# Revit family: RN 90032 Optifitt-Serra-Rohrnippel
name_source: partatom
category: Rohrformteile
units: mm (PartAtom-declared; Revit-internal decimal feet)

## family parameters
Arbeitsebenenbasiert = Nein
Beim Laden mit Abzugskörper schneiden = Nein
Bemaßung runder Anschluss = Durchmesser verwenden
Gemeinsam genutzt = Nein
Immer vertikal = Ja
Teiletyp = Nicht definiert

## types (17) — shared parameters
1.010.00.2 Blattnummer der Richtlinie = 29
1.010.00.3 Ausgabedatum (Monat) der Richtlinie = 201308
1.010.00.4 Herstellername = R. Nussbaum AG
1.010.00.5 Revisionsdatum der Datei = 20190521
1.010.00.6 Webadresse des Herstellers = http://www.nussbaum.ch
1.100.00.4 Produktbezeichnung = Versorgung
1.110.00.2 Index = 3
1.110.00.4 Produktbezeichnung = Optifitt-Serra
1.960/3L.00.8 Link (URL) = https://www.nussbaum.ch
29.700.00.4 Produktname = Optifitt-Serra-Rohrnippel
29.700.00.5 Produktkennung = 2
29.700.00.6 Querschnittsform = 1
29.700.00.7 Nennweitensystem = DN
29.700.00.8 Nenndrucksystem = PN
29.710.02.4 Nenndruck = 16
29.710.02.5 max. zul. Überdruck [hPa] = 1600
29.710.02.7 max. zul. Dauer-Betriebsdruck [hPa] = 1600
29.710.02.9 max. zul. Dauer-Betriebstemperatur [°C] = 90
Connector Visibility = Nein
EnclosingSpace Visibility = Nein
R. Nussbaum AG 90032.22 de Visibility = Nein
R. Nussbaum AG 90032.24 de Visibility = Nein
R. Nussbaum AG 90032.26 de Visibility = Nein
R. Nussbaum AG 90032.28 de Visibility = Nein
R. Nussbaum AG 90032.30 de Visibility = Nein
R. Nussbaum AG 90032.32 de Visibility = Nein
R. Nussbaum AG 90032.34 de Visibility = Nein
R. Nussbaum AG 90032.38 de Visibility = Nein
R. Nussbaum AG 90032.39 de Visibility = Nein
R. Nussbaum AG 90032.41 de Visibility = Nein
R. Nussbaum AG 90032.42 de Visibility = Nein
R. Nussbaum AG 90032.44 de Visibility = Nein
R. Nussbaum AG 90032.45 de Visibility = Nein
R. Nussbaum AG 90032.46 de Visibility = Nein
R. Nussbaum AG 90032.49 de Visibility = Nein
R. Nussbaum AG 90032.51 de Visibility = Nein
R. Nussbaum AG 90032.52 de Visibility = Nein
R. Nussbaum AG 90032.53 de Visibility = Nein
R. Nussbaum AG 90032.54 de Visibility = Nein
R. Nussbaum AG 90032.56 de Visibility = Nein
R. Nussbaum AG 90032.58 de Visibility = Nein
R. Nussbaum AG 90032.59 de Visibility = Nein
R. Nussbaum AG 90032.61 de Visibility = Nein
R. Nussbaum AG 90032.62 de Visibility = Nein
R. Nussbaum AG 90032.63 de Visibility = Nein
R. Nussbaum AG 90032.64 de Visibility = Nein
R. Nussbaum AG 90032.66 de Visibility = Nein
R. Nussbaum AG 90032.67 de Visibility = Nein
R. Nussbaum AG 90032.68 de Visibility = Nein
R. Nussbaum AG 90032.69 de Visibility = Nein
R. Nussbaum AG 90032.71 de Visibility = Nein
R. Nussbaum AG 90032.72 de Visibility = Nein
R. Nussbaum AG 90032.74 de Visibility = Nein
R. Nussbaum AG 90032.75 de Visibility = Nein
R. Nussbaum AG 90032.78 de Visibility = Nein
R. Nussbaum AG 90032.79 de Visibility = Nein
R. Nussbaum AG 90032.82 de Visibility = Nein
R. Nussbaum AG 90032.83 de Visibility = Nein
R. Nussbaum AG 90032.86 de Visibility = Nein
R. Nussbaum AG 90032.87 de Visibility = Nein
R. Nussbaum AG 90032.89 de Visibility = Nein
R. Nussbaum AG 90032.90 de Visibility = Nein
R. Nussbaum AG 90032.91 de Visibility = Nein
R. Nussbaum AG 90032.94 de Visibility = Nein
R. Nussbaum AG 90032.95 de Visibility = Nein
R. Nussbaum AG 90032.96 de Visibility = Nein
R. Nussbaum AG 90032.97 de Visibility = Nein

## per-type parameters (varying)
- DN=40: 1.800.00.3 TGA-Nummer=01900300000000000000000000000000000000000000000019000000000000000048; 1.800.00.4 Kommentarfeld=90032.88, Optifitt-Serra-Rohrnippel, DN=40, L=100, R=1½; 1.810.00.3 Hersteller-Bestellnummer=90032.88; 1.810.00.4 DATANORM-Nummer=90032.88; 1.810.00.5 StLB-Nummer=214.236; 1.810.00.6 GTIN-Nummer=7612945034571; 29.710.02.10 Formstück-Gewicht [kg]=0.459; 29.710.02.3 Benennung=Optifitt-Serra-Rohrnippel, DN=40, L=100, R=1½; CONNECTOR0_DIAMETER_dX_0r=40 mm; CONNECTOR0_dX_01=19 mm  [stored 0.062336 ft]; CONNECTOR0_ref_dX=19 mm  [stored 0.062336 ft]; CONNECTOR1_DIAMETER_dX_0r=40 mm; CONNECTOR1_dX_00=79 mm; CONNECTOR1_dX_01=98 mm; CONNECTOR1_ref_dX=79 mm; CONNECTOR1_ref_dX2=98 mm; R. Nussbaum AG 90032.36 de Visibility=Nein; R. Nussbaum AG 90032.37 de Visibility=Nein; R. Nussbaum AG 90032.40 de Visibility=Nein; R. Nussbaum AG 90032.47 de Visibility=Nein; R. Nussbaum AG 90032.48 de Visibility=Nein; R. Nussbaum AG 90032.50 de Visibility=Nein; R. Nussbaum AG 90032.55 de Visibility=Nein; R. Nussbaum AG 90032.57 de Visibility=Nein; R. Nussbaum AG 90032.60 de Visibility=Nein; R. Nussbaum AG 90032.65 de Visibility=Nein; R. Nussbaum AG 90032.70 de Visibility=Nein; R. Nussbaum AG 90032.80 de Visibility=Nein; R. Nussbaum AG 90032.81 de Visibility=Nein; R. Nussbaum AG 90032.88 de Visibility=Ja; R. Nussbaum AG 90032.93 de Visibility=Nein; R. Nussbaum AG 90032.98 de Visibility=Nein; R. Nussbaum AG 90032.99 de Visibility=Nein
- DN=4: 1.800.00.3 TGA-Nummer=01900300000000000000000000000000000000000000000019000000000000000073; 1.800.00.4 Kommentarfeld=90032.80, Optifitt-Serra-Rohrnippel, DN=32, L=100, R=1¼; 1.810.00.3 Hersteller-Bestellnummer=90032.8; 1.810.00.4 DATANORM-Nummer=90032.8; 1.810.00.5 StLB-Nummer=214.235; 1.810.00.6 GTIN-Nummer=7612945034519; 29.710.02.10 Formstück-Gewicht [kg]=0.41; 29.710.02.3 Benennung=Optifitt-Serra-Rohrnippel, DN=32, L=100, R=1¼; CONNECTOR0_DIAMETER_dX_0r=32 mm  [stored 0.104987 ft]; CONNECTOR0_dX_01=19 mm  [stored 0.062336 ft]; CONNECTOR0_ref_dX=19 mm  [stored 0.062336 ft]; CONNECTOR1_DIAMETER_dX_0r=32 mm  [stored 0.104987 ft]; CONNECTOR1_dX_00=79 mm; CONNECTOR1_dX_01=98 mm; CONNECTOR1_ref_dX=79 mm; CONNECTOR1_ref_dX2=98 mm; Hersteller=R. Nussbaum AG; Modell=90032.8; R. Nussbaum AG 90032.36 de Visibility=Nein; R. Nussbaum AG 90032.37 de Visibility=Nein; R. Nussbaum AG 90032.40 de Visibility=Nein; R. Nussbaum AG 90032.47 de Visibility=Nein; R. Nussbaum AG 90032.48 de Visibility=Nein; R. Nussbaum AG 90032.50 de Visibility=Nein; R. Nussbaum AG 90032.55 de Visibility=Nein; R. Nussbaum AG 90032.57 de Visibility=Nein; R. Nussbaum AG 90032.60 de Visibility=Nein; R. Nussbaum AG 90032.65 de Visibility=Nein; R. Nussbaum AG 90032.70 de Visibility=Nein; R. Nussbaum AG 90032.80 de Visibility=Ja; R. Nussbaum AG 90032.81 de Visibility=Nein; R. Nussbaum AG 90032.88 de Visibility=Nein; R. Nussbaum AG 90032.93 de Visibility=Nein; R. Nussbaum AG 90032.98 de Visibility=Nein; R. Nussbaum AG 90032.99 de Visibility=Nein; Typenkommentare=Optifitt-Serra-Rohrnippel  DN=32; URL=https://www.nussbaum.ch
- DN=3: 1.800.00.3 TGA-Nummer=01900300000000000000000000000000000000000000000019000000000000000072; 1.800.00.4 Kommentarfeld=90032.70, Optifitt-Serra-Rohrnippel, DN=25, L=100, R=1; 1.810.00.3 Hersteller-Bestellnummer=90032.7; 1.810.00.4 DATANORM-Nummer=90032.7; 1.810.00.5 StLB-Nummer=214.234; 1.810.00.6 GTIN-Nummer=7612945034458; 29.710.02.10 Formstück-Gewicht [kg]=0.287; 29.710.02.3 Benennung=Optifitt-Serra-Rohrnippel, DN=25, L=100, R=1; CONNECTOR0_DIAMETER_dX_0r=25 mm  [stored 0.082021 ft]; CONNECTOR0_dX_01=17 mm; CONNECTOR0_ref_dX=17 mm; CONNECTOR1_DIAMETER_dX_0r=25 mm  [stored 0.082021 ft]; CONNECTOR1_dX_00=81 mm; CONNECTOR1_dX_01=98 mm; CONNECTOR1_ref_dX=81 mm; CONNECTOR1_ref_dX2=98 mm; Hersteller=R. Nussbaum AG; Modell=90032.7; R. Nussbaum AG 90032.36 de Visibility=Nein; R. Nussbaum AG 90032.37 de Visibility=Nein; R. Nussbaum AG 90032.40 de Visibility=Nein; R. Nussbaum AG 90032.47 de Visibility=Nein; R. Nussbaum AG 90032.48 de Visibility=Nein; R. Nussbaum AG 90032.50 de Visibility=Nein; R. Nussbaum AG 90032.55 de Visibility=Nein; R. Nussbaum AG 90032.57 de Visibility=Nein; R. Nussbaum AG 90032.60 de Visibility=Nein; R. Nussbaum AG 90032.65 de Visibility=Nein; R. Nussbaum AG 90032.70 de Visibility=Ja; R. Nussbaum AG 90032.80 de Visibility=Nein; R. Nussbaum AG 90032.81 de Visibility=Nein; R. Nussbaum AG 90032.88 de Visibility=Nein; R. Nussbaum AG 90032.93 de Visibility=Nein; R. Nussbaum AG 90032.98 de Visibility=Nein; R. Nussbaum AG 90032.99 de Visibility=Nein; Typenkommentare=Optifitt-Serra-Rohrnippel  DN=25; URL=https://www.nussbaum.ch
- DN=2: 1.800.00.3 TGA-Nummer=01900300000000000000000000000000000000000000000019000000000000000071; 1.800.00.4 Kommentarfeld=90032.60, Optifitt-Serra-Rohrnippel, DN=20, L=150, R=¾; 1.810.00.3 Hersteller-Bestellnummer=90032.6; 1.810.00.4 DATANORM-Nummer=90032.6; 1.810.00.6 GTIN-Nummer=7612945034380; 29.710.02.10 Formstück-Gewicht [kg]=0.325; 29.710.02.3 Benennung=Optifitt-Serra-Rohrnippel, DN=20, L=150, R=¾; CONNECTOR0_DIAMETER_dX_0r=20 mm  [stored 0.0656168 ft]; CONNECTOR0_dX_01=15 mm  [stored 0.0492126 ft]; CONNECTOR0_ref_dX=15 mm  [stored 0.0492126 ft]; CONNECTOR1_DIAMETER_dX_0r=20 mm  [stored 0.0656168 ft]; CONNECTOR1_dX_00=133 mm; CONNECTOR1_dX_01=148 mm; CONNECTOR1_ref_dX=133 mm; CONNECTOR1_ref_dX2=148 mm; Hersteller=R. Nussbaum AG; Modell=90032.6; R. Nussbaum AG 90032.36 de Visibility=Nein; R. Nussbaum AG 90032.37 de Visibility=Nein; R. Nussbaum AG 90032.40 de Visibility=Nein; R. Nussbaum AG 90032.47 de Visibility=Nein; R. Nussbaum AG 90032.48 de Visibility=Nein; R. Nussbaum AG 90032.50 de Visibility=Nein; R. Nussbaum AG 90032.55 de Visibility=Nein; R. Nussbaum AG 90032.57 de Visibility=Nein; R. Nussbaum AG 90032.60 de Visibility=Ja; R. Nussbaum AG 90032.65 de Visibility=Nein; R. Nussbaum AG 90032.70 de Visibility=Nein; R. Nussbaum AG 90032.80 de Visibility=Nein; R. Nussbaum AG 90032.81 de Visibility=Nein; R. Nussbaum AG 90032.88 de Visibility=Nein; R. Nussbaum AG 90032.93 de Visibility=Nein; R. Nussbaum AG 90032.98 de Visibility=Nein; R. Nussbaum AG 90032.99 de Visibility=Nein; Typenkommentare=Optifitt-Serra-Rohrnippel  DN=20; URL=https://www.nussbaum.ch
- DN=5: 1.800.00.3 TGA-Nummer=01900300000000000000000000000000000000000000000019000000000000000070; 1.800.00.4 Kommentarfeld=90032.50, Optifitt-Serra-Rohrnippel, DN=20, L=40, R=¾; 1.810.00.3 Hersteller-Bestellnummer=90032.5; 1.810.00.4 DATANORM-Nummer=90032.5; 1.810.00.5 StLB-Nummer=214.233; 1.810.00.6 GTIN-Nummer=7612945034328; 29.710.02.10 Formstück-Gewicht [kg]=0.072; 29.710.02.3 Benennung=Optifitt-Serra-Rohrnippel, DN=20, L=40, R=¾; CONNECTOR0_DIAMETER_dX_0r=20 mm  [stored 0.0656168 ft]; CONNECTOR0_dX_01=15 mm  [stored 0.0492126 ft]; CONNECTOR0_ref_dX=15 mm  [stored 0.0492126 ft]; CONNECTOR1_DIAMETER_dX_0r=20 mm  [stored 0.0656168 ft]; CONNECTOR1_dX_00=23 mm  [stored 0.0754593 ft]; CONNECTOR1_dX_01=38 mm; CONNECTOR1_ref_dX=23 mm  [stored 0.0754593 ft]; CONNECTOR1_ref_dX2=38 mm; Hersteller=R. Nussbaum AG; Modell=90032.5; R. Nussbaum AG 90032.36 de Visibility=Nein; R. Nussbaum AG 90032.37 de Visibility=Nein; R. Nussbaum AG 90032.40 de Visibility=Nein; R. Nussbaum AG 90032.47 de Visibility=Nein; R. Nussbaum AG 90032.48 de Visibility=Nein; R. Nussbaum AG 90032.50 de Visibility=Ja; R. Nussbaum AG 90032.55 de Visibility=Nein; R. Nussbaum AG 90032.57 de Visibility=Nein; R. Nussbaum AG 90032.60 de Visibility=Nein; R. Nussbaum AG 90032.65 de Visibility=Nein; R. Nussbaum AG 90032.70 de Visibility=Nein; R. Nussbaum AG 90032.80 de Visibility=Nein; R. Nussbaum AG 90032.81 de Visibility=Nein; R. Nussbaum AG 90032.88 de Visibility=Nein; R. Nussbaum AG 90032.93 de Visibility=Nein; R. Nussbaum AG 90032.98 de Visibility=Nein; R. Nussbaum AG 90032.99 de Visibility=Nein; Typenkommentare=Optifitt-Serra-Rohrnippel  DN=20; URL=https://www.nussbaum.ch
- DN=7: 1.800.00.3 TGA-Nummer=01900300000000000000000000000000000000000000000019000000000000000069; 1.800.00.4 Kommentarfeld=90032.40, Optifitt-Serra-Rohrnippel, DN=15, L=80, R=½; 1.810.00.3 Hersteller-Bestellnummer=90032.4; 1.810.00.4 DATANORM-Nummer=90032.4; 1.810.00.6 GTIN-Nummer=7612945034243; 29.710.02.10 Formstück-Gewicht [kg]=0.13; 29.710.02.3 Benennung=Optifitt-Serra-Rohrnippel, DN=15, L=80, R=½; CONNECTOR0_DIAMETER_dX_0r=15 mm  [stored 0.0492126 ft]; CONNECTOR0_dX_01=13 mm; CONNECTOR0_ref_dX=13 mm; CONNECTOR1_DIAMETER_dX_0r=15 mm  [stored 0.0492126 ft]; CONNECTOR1_dX_00=65 mm; CONNECTOR1_dX_01=78 mm  [stored 0.255906 ft]; CONNECTOR1_ref_dX=65 mm; CONNECTOR1_ref_dX2=78 mm  [stored 0.255906 ft]; Hersteller=R. Nussbaum AG; Modell=90032.4; R. Nussbaum AG 90032.36 de Visibility=Nein; R. Nussbaum AG 90032.37 de Visibility=Nein; R. Nussbaum AG 90032.40 de Visibility=Ja; R. Nussbaum AG 90032.47 de Visibility=Nein; R. Nussbaum AG 90032.48 de Visibility=Nein; R. Nussbaum AG 90032.50 de Visibility=Nein; R. Nussbaum AG 90032.55 de Visibility=Nein; R. Nussbaum AG 90032.57 de Visibility=Nein; R. Nussbaum AG 90032.60 de Visibility=Nein; R. Nussbaum AG 90032.65 de Visibility=Nein; R. Nussbaum AG 90032.70 de Visibility=Nein; R. Nussbaum AG 90032.80 de Visibility=Nein; R. Nussbaum AG 90032.81 de Visibility=Nein; R. Nussbaum AG 90032.88 de Visibility=Nein; R. Nussbaum AG 90032.93 de Visibility=Nein; R. Nussbaum AG 90032.98 de Visibility=Nein; R. Nussbaum AG 90032.99 de Visibility=Nein; Typenkommentare=Optifitt-Serra-Rohrnippel  DN=15; URL=https://www.nussbaum.ch
- DN=50: 1.800.00.3 TGA-Nummer=01900300000000000000000000000000000000000000000019000000000000000057; 1.800.00.4 Kommentarfeld=90032.99, Optifitt-Serra-Rohrnippel, DN=50, L=200, R=2; 1.810.00.3 Hersteller-Bestellnummer=90032.99; 1.810.00.4 DATANORM-Nummer=90032.99; 1.810.00.6 GTIN-Nummer=7612945034663; 29.710.02.10 Formstück-Gewicht [kg]=1.159; 29.710.02.3 Benennung=Optifitt-Serra-Rohrnippel, DN=50, L=200, R=2; CONNECTOR0_DIAMETER_dX_0r=50 mm  [stored 0.164042 ft]; CONNECTOR0_dX_01=24 mm; CONNECTOR0_ref_dX=24 mm; CONNECTOR1_DIAMETER_dX_0r=50 mm  [stored 0.164042 ft]; CONNECTOR1_dX_00=174 mm; CONNECTOR1_dX_01=198 mm  [stored 0.649606 ft]; CONNECTOR1_ref_dX=174 mm; CONNECTOR1_ref_dX2=198 mm  [stored 0.649606 ft]; Hersteller=R. Nussbaum AG; Modell=90032.99; R. Nussbaum AG 90032.36 de Visibility=Nein; R. Nussbaum AG 90032.37 de Visibility=Nein; R. Nussbaum AG 90032.40 de Visibility=Nein; R. Nussbaum AG 90032.47 de Visibility=Nein; R. Nussbaum AG 90032.48 de Visibility=Nein; R. Nussbaum AG 90032.50 de Visibility=Nein; R. Nussbaum AG 90032.55 de Visibility=Nein; R. Nussbaum AG 90032.57 de Visibility=Nein; R. Nussbaum AG 90032.60 de Visibility=Nein; R. Nussbaum AG 90032.65 de Visibility=Nein; R. Nussbaum AG 90032.70 de Visibility=Nein; R. Nussbaum AG 90032.80 de Visibility=Nein; R. Nussbaum AG 90032.81 de Visibility=Nein; R. Nussbaum AG 90032.88 de Visibility=Nein; R. Nussbaum AG 90032.93 de Visibility=Nein; R. Nussbaum AG 90032.98 de Visibility=Nein; R. Nussbaum AG 90032.99 de Visibility=Ja; Typenkommentare=Optifitt-Serra-Rohrnippel  DN=50; URL=https://www.nussbaum.ch
- DN=6: 1.800.00.3 TGA-Nummer=01900300000000000000000000000000000000000000000019000000000000000056; 1.800.00.4 Kommentarfeld=90032.98, Optifitt-Serra-Rohrnippel, DN=50, L=150, R=2; 1.810.00.3 Hersteller-Bestellnummer=90032.98; 1.810.00.4 DATANORM-Nummer=90032.98; 1.810.00.6 GTIN-Nummer=7612945034656; 29.710.02.10 Formstück-Gewicht [kg]=0.837; 29.710.02.3 Benennung=Optifitt-Serra-Rohrnippel, DN=50, L=150, R=2; CONNECTOR0_DIAMETER_dX_0r=50 mm  [stored 0.164042 ft]; CONNECTOR0_dX_01=24 mm; CONNECTOR0_ref_dX=24 mm; CONNECTOR1_DIAMETER_dX_0r=50 mm  [stored 0.164042 ft]; CONNECTOR1_dX_00=124 mm  [stored 0.406824 ft]; CONNECTOR1_dX_01=148 mm; CONNECTOR1_ref_dX=124 mm  [stored 0.406824 ft]; CONNECTOR1_ref_dX2=148 mm; Hersteller=R. Nussbaum AG; Modell=90032.98; R. Nussbaum AG 90032.36 de Visibility=Nein; R. Nussbaum AG 90032.37 de Visibility=Nein; R. Nussbaum AG 90032.40 de Visibility=Nein; R. Nussbaum AG 90032.47 de Visibility=Nein; R. Nussbaum AG 90032.48 de Visibility=Nein; R. Nussbaum AG 90032.50 de Visibility=Nein; R. Nussbaum AG 90032.55 de Visibility=Nein; R. Nussbaum AG 90032.57 de Visibility=Nein; R. Nussbaum AG 90032.60 de Visibility=Nein; R. Nussbaum AG 90032.65 de Visibility=Nein; R. Nussbaum AG 90032.70 de Visibility=Nein; R. Nussbaum AG 90032.80 de Visibility=Nein; R. Nussbaum AG 90032.81 de Visibility=Nein; R. Nussbaum AG 90032.88 de Visibility=Nein; R. Nussbaum AG 90032.93 de Visibility=Nein; R. Nussbaum AG 90032.98 de Visibility=Ja; R. Nussbaum AG 90032.99 de Visibility=Nein; Typenkommentare=Optifitt-Serra-Rohrnippel  DN=50; URL=https://www.nussbaum.ch
- DN=65: 1.800.00.3 TGA-Nummer=01900300000000000000000000000000000000000000000019000000000000000051; 1.800.00.4 Kommentarfeld=90032.93, Optifitt-Serra-Rohrnippel, DN=65, L=100, R=2½; 1.810.00.3 Hersteller-Bestellnummer=90032.93; 1.810.00.4 DATANORM-Nummer=90032.93; 1.810.00.5 StLB-Nummer=214.238; 1.810.00.6 GTIN-Nummer=7612945613387; 29.710.02.10 Formstück-Gewicht [kg]=1.042; 29.710.02.3 Benennung=Optifitt-Serra-Rohrnippel, DN=65, L=100, R=2½; CONNECTOR0_DIAMETER_dX_0r=65 mm; CONNECTOR0_dX_01=27 mm; CONNECTOR0_ref_dX=27 mm; CONNECTOR1_DIAMETER_dX_0r=65 mm; CONNECTOR1_dX_00=73 mm  [stored 0.239501 ft]; CONNECTOR1_dX_01=100 mm  [stored 0.328084 ft]; CONNECTOR1_ref_dX=73 mm  [stored 0.239501 ft]; CONNECTOR1_ref_dX2=100 mm  [stored 0.328084 ft]; R. Nussbaum AG 90032.36 de Visibility=Nein; R. Nussbaum AG 90032.37 de Visibility=Nein; R. Nussbaum AG 90032.40 de Visibility=Nein; R. Nussbaum AG 90032.47 de Visibility=Nein; R. Nussbaum AG 90032.48 de Visibility=Nein; R. Nussbaum AG 90032.50 de Visibility=Nein; R. Nussbaum AG 90032.55 de Visibility=Nein; R. Nussbaum AG 90032.57 de Visibility=Nein; R. Nussbaum AG 90032.60 de Visibility=Nein; R. Nussbaum AG 90032.65 de Visibility=Nein; R. Nussbaum AG 90032.70 de Visibility=Nein; R. Nussbaum AG 90032.80 de Visibility=Nein; R. Nussbaum AG 90032.81 de Visibility=Nein; R. Nussbaum AG 90032.88 de Visibility=Nein; R. Nussbaum AG 90032.93 de Visibility=Ja; R. Nussbaum AG 90032.98 de Visibility=Nein; R. Nussbaum AG 90032.99 de Visibility=Nein
- DN=32: 1.800.00.3 TGA-Nummer=01900300000000000000000000000000000000000000000019000000000000000043; 1.800.00.4 Kommentarfeld=90032.81, Optifitt-Serra-Rohrnippel, DN=32, L=120, R=1¼; 1.810.00.3 Hersteller-Bestellnummer=90032.81; 1.810.00.4 DATANORM-Nummer=90032.81; 1.810.00.5 StLB-Nummer=214.235; 1.810.00.6 GTIN-Nummer=7612945034526; 29.710.02.10 Formstück-Gewicht [kg]=0.483; 29.710.02.3 Benennung=Optifitt-Serra-Rohrnippel, DN=32, L=120, R=1¼; CONNECTOR0_DIAMETER_dX_0r=32 mm  [stored 0.104987 ft]; CONNECTOR0_dX_01=19 mm  [stored 0.062336 ft]; CONNECTOR0_ref_dX=19 mm  [stored 0.062336 ft]; CONNECTOR1_DIAMETER_dX_0r=32 mm  [stored 0.104987 ft]; CONNECTOR1_dX_00=99 mm  [stored 0.324803 ft]; CONNECTOR1_dX_01=118 mm; CONNECTOR1_ref_dX=99 mm  [stored 0.324803 ft]; CONNECTOR1_ref_dX2=118 mm; R. Nussbaum AG 90032.36 de Visibility=Nein; R. Nussbaum AG 90032.37 de Visibility=Nein; R. Nussbaum AG 90032.40 de Visibility=Nein; R. Nussbaum AG 90032.47 de Visibility=Nein; R. Nussbaum AG 90032.48 de Visibility=Nein; R. Nussbaum AG 90032.50 de Visibility=Nein; R. Nussbaum AG 90032.55 de Visibility=Nein; R. Nussbaum AG 90032.57 de Visibility=Nein; R. Nussbaum AG 90032.60 de Visibility=Nein; R. Nussbaum AG 90032.65 de Visibility=Nein; R. Nussbaum AG 90032.70 de Visibility=Nein; R. Nussbaum AG 90032.80 de Visibility=Nein; R. Nussbaum AG 90032.81 de Visibility=Ja; R. Nussbaum AG 90032.88 de Visibility=Nein; R. Nussbaum AG 90032.93 de Visibility=Nein; R. Nussbaum AG 90032.98 de Visibility=Nein; R. Nussbaum AG 90032.99 de Visibility=Nein
- DN=25: 1.800.00.3 TGA-Nummer=01900300000000000000000000000000000000000000000019000000000000000032; 1.800.00.4 Kommentarfeld=90032.65, Optifitt-Serra-Rohrnippel, DN=25, L=50, R=1; 1.810.00.3 Hersteller-Bestellnummer=90032.65; 1.810.00.4 DATANORM-Nummer=90032.65; 1.810.00.6 GTIN-Nummer=7612945697820; 29.710.02.10 Formstück-Gewicht [kg]=0.121; 29.710.02.3 Benennung=Optifitt-Serra-Rohrnippel, DN=25, L=50, R=1; CONNECTOR0_DIAMETER_dX_0r=25 mm  [stored 0.082021 ft]; CONNECTOR0_dX_01=17 mm; CONNECTOR0_ref_dX=17 mm; CONNECTOR1_DIAMETER_dX_0r=25 mm  [stored 0.082021 ft]; CONNECTOR1_dX_00=31 mm; CONNECTOR1_dX_01=48 mm  [stored 0.15748 ft]; CONNECTOR1_ref_dX=31 mm; CONNECTOR1_ref_dX2=48 mm  [stored 0.15748 ft]; R. Nussbaum AG 90032.36 de Visibility=Nein; R. Nussbaum AG 90032.37 de Visibility=Nein; R. Nussbaum AG 90032.40 de Visibility=Nein; R. Nussbaum AG 90032.47 de Visibility=Nein; R. Nussbaum AG 90032.48 de Visibility=Nein; R. Nussbaum AG 90032.50 de Visibility=Nein; R. Nussbaum AG 90032.55 de Visibility=Nein; R. Nussbaum AG 90032.57 de Visibility=Nein; R. Nussbaum AG 90032.60 de Visibility=Nein; R. Nussbaum AG 90032.65 de Visibility=Ja; R. Nussbaum AG 90032.70 de Visibility=Nein; R. Nussbaum AG 90032.80 de Visibility=Nein; R. Nussbaum AG 90032.81 de Visibility=Nein; R. Nussbaum AG 90032.88 de Visibility=Nein; R. Nussbaum AG 90032.93 de Visibility=Nein; R. Nussbaum AG 90032.98 de Visibility=Nein; R. Nussbaum AG 90032.99 de Visibility=Nein
- DN=20: 1.800.00.3 TGA-Nummer=01900300000000000000000000000000000000000000000019000000000000000025; 1.800.00.4 Kommentarfeld=90032.57, Optifitt-Serra-Rohrnippel, DN=20, L=110, R=¾; 1.810.00.3 Hersteller-Bestellnummer=90032.57; 1.810.00.4 DATANORM-Nummer=90032.57; 1.810.00.6 GTIN-Nummer=7612945723628; 29.710.02.10 Formstück-Gewicht [kg]=0.229; 29.710.02.3 Benennung=Optifitt-Serra-Rohrnippel, DN=20, L=110, R=¾; CONNECTOR0_DIAMETER_dX_0r=20 mm  [stored 0.0656168 ft]; CONNECTOR0_dX_01=15 mm  [stored 0.0492126 ft]; CONNECTOR0_ref_dX=15 mm  [stored 0.0492126 ft]; CONNECTOR1_DIAMETER_dX_0r=20 mm  [stored 0.0656168 ft]; CONNECTOR1_dX_00=93 mm  [stored 0.305118 ft]; CONNECTOR1_dX_01=108 mm  [stored 0.354331 ft]; CONNECTOR1_ref_dX=93 mm  [stored 0.305118 ft]; CONNECTOR1_ref_dX2=108 mm  [stored 0.354331 ft]; R. Nussbaum AG 90032.36 de Visibility=Nein; R. Nussbaum AG 90032.37 de Visibility=Nein; R. Nussbaum AG 90032.40 de Visibility=Nein; R. Nussbaum AG 90032.47 de Visibility=Nein; R. Nussbaum AG 90032.48 de Visibility=Nein; R. Nussbaum AG 90032.50 de Visibility=Nein; R. Nussbaum AG 90032.55 de Visibility=Nein; R. Nussbaum AG 90032.57 de Visibility=Ja; R. Nussbaum AG 90032.60 de Visibility=Nein; R. Nussbaum AG 90032.65 de Visibility=Nein; R. Nussbaum AG 90032.70 de Visibility=Nein; R. Nussbaum AG 90032.80 de Visibility=Nein; R. Nussbaum AG 90032.81 de Visibility=Nein; R. Nussbaum AG 90032.88 de Visibility=Nein; R. Nussbaum AG 90032.93 de Visibility=Nein; R. Nussbaum AG 90032.98 de Visibility=Nein; R. Nussbaum AG 90032.99 de Visibility=Nein
- DN=8: 1.800.00.3 TGA-Nummer=01900300000000000000000000000000000000000000000019000000000000000023; 1.800.00.4 Kommentarfeld=90032.55, Optifitt-Serra-Rohrnippel, DN=20, L=90, R=¾; 1.810.00.3 Hersteller-Bestellnummer=90032.55; 1.810.00.4 DATANORM-Nummer=90032.55; 1.810.00.6 GTIN-Nummer=7612945697806; 29.710.02.10 Formstück-Gewicht [kg]=0.181; 29.710.02.3 Benennung=Optifitt-Serra-Rohrnippel, DN=20, L=90, R=¾; CONNECTOR0_DIAMETER_dX_0r=20 mm  [stored 0.0656168 ft]; CONNECTOR0_dX_01=15 mm  [stored 0.0492126 ft]; CONNECTOR0_ref_dX=15 mm  [stored 0.0492126 ft]; CONNECTOR1_DIAMETER_dX_0r=20 mm  [stored 0.0656168 ft]; CONNECTOR1_dX_00=73 mm  [stored 0.239501 ft]; CONNECTOR1_dX_01=88 mm  [stored 0.288714 ft]; CONNECTOR1_ref_dX=73 mm  [stored 0.239501 ft]; CONNECTOR1_ref_dX2=88 mm  [stored 0.288714 ft]; Hersteller=R. Nussbaum AG; Modell=90032.55; R. Nussbaum AG 90032.36 de Visibility=Nein; R. Nussbaum AG 90032.37 de Visibility=Nein; R. Nussbaum AG 90032.40 de Visibility=Nein; R. Nussbaum AG 90032.47 de Visibility=Nein; R. Nussbaum AG 90032.48 de Visibility=Nein; R. Nussbaum AG 90032.50 de Visibility=Nein; R. Nussbaum AG 90032.55 de Visibility=Ja; R. Nussbaum AG 90032.57 de Visibility=Nein; R. Nussbaum AG 90032.60 de Visibility=Nein; R. Nussbaum AG 90032.65 de Visibility=Nein; R. Nussbaum AG 90032.70 de Visibility=Nein; R. Nussbaum AG 90032.80 de Visibility=Nein; R. Nussbaum AG 90032.81 de Visibility=Nein; R. Nussbaum AG 90032.88 de Visibility=Nein; R. Nussbaum AG 90032.93 de Visibility=Nein; R. Nussbaum AG 90032.98 de Visibility=Nein; R. Nussbaum AG 90032.99 de Visibility=Nein; Typenkommentare=Optifitt-Serra-Rohrnippel  DN=20; URL=https://www.nussbaum.ch
- DN=15: 1.800.00.3 TGA-Nummer=01900300000000000000000000000000000000000000000019000000000000000008; 1.800.00.4 Kommentarfeld=90032.37, Optifitt-Serra-Rohrnippel, DN=15, L=50, R=½; 1.810.00.3 Hersteller-Bestellnummer=90032.37; 1.810.00.4 DATANORM-Nummer=90032.37; 1.810.00.6 GTIN-Nummer=7612945697707; 29.710.02.10 Formstück-Gewicht [kg]=0.073; 29.710.02.3 Benennung=Optifitt-Serra-Rohrnippel, DN=15, L=50, R=½; CONNECTOR0_DIAMETER_dX_0r=15 mm  [stored 0.0492126 ft]; CONNECTOR0_dX_01=13 mm; CONNECTOR0_ref_dX=13 mm; CONNECTOR1_DIAMETER_dX_0r=15 mm  [stored 0.0492126 ft]; CONNECTOR1_dX_00=35 mm; CONNECTOR1_dX_01=48 mm  [stored 0.15748 ft]; CONNECTOR1_ref_dX=35 mm; CONNECTOR1_ref_dX2=48 mm  [stored 0.15748 ft]; R. Nussbaum AG 90032.36 de Visibility=Nein; R. Nussbaum AG 90032.37 de Visibility=Ja; R. Nussbaum AG 90032.40 de Visibility=Nein; R. Nussbaum AG 90032.47 de Visibility=Nein; R. Nussbaum AG 90032.48 de Visibility=Nein; R. Nussbaum AG 90032.50 de Visibility=Nein; R. Nussbaum AG 90032.55 de Visibility=Nein; R. Nussbaum AG 90032.57 de Visibility=Nein; R. Nussbaum AG 90032.60 de Visibility=Nein; R. Nussbaum AG 90032.65 de Visibility=Nein; R. Nussbaum AG 90032.70 de Visibility=Nein; R. Nussbaum AG 90032.80 de Visibility=Nein; R. Nussbaum AG 90032.81 de Visibility=Nein; R. Nussbaum AG 90032.88 de Visibility=Nein; R. Nussbaum AG 90032.93 de Visibility=Nein; R. Nussbaum AG 90032.98 de Visibility=Nein; R. Nussbaum AG 90032.99 de Visibility=Nein
- DN=9: 1.800.00.3 TGA-Nummer=01900300000000000000000000000000000000000000000019000000000000000017; 1.800.00.4 Kommentarfeld=90032.48, Optifitt-Serra-Rohrnippel, DN=15, L=200, R=½; 1.810.00.3 Hersteller-Bestellnummer=90032.48; 1.810.00.4 DATANORM-Nummer=90032.48; 1.810.00.6 GTIN-Nummer=7612945034304; 29.710.02.10 Formstück-Gewicht [kg]=0.343; 29.710.02.3 Benennung=Optifitt-Serra-Rohrnippel, DN=15, L=200, R=½; CONNECTOR0_DIAMETER_dX_0r=15 mm  [stored 0.0492126 ft]; CONNECTOR0_dX_01=13 mm; CONNECTOR0_ref_dX=13 mm; CONNECTOR1_DIAMETER_dX_0r=15 mm  [stored 0.0492126 ft]; CONNECTOR1_dX_00=185 mm; CONNECTOR1_dX_01=198 mm  [stored 0.649606 ft]; CONNECTOR1_ref_dX=185 mm; CONNECTOR1_ref_dX2=198 mm  [stored 0.649606 ft]; Hersteller=R. Nussbaum AG; Modell=90032.48; R. Nussbaum AG 90032.36 de Visibility=Nein; R. Nussbaum AG 90032.37 de Visibility=Nein; R. Nussbaum AG 90032.40 de Visibility=Nein; R. Nussbaum AG 90032.47 de Visibility=Nein; R. Nussbaum AG 90032.48 de Visibility=Ja; R. Nussbaum AG 90032.50 de Visibility=Nein; R. Nussbaum AG 90032.55 de Visibility=Nein; R. Nussbaum AG 90032.57 de Visibility=Nein; R. Nussbaum AG 90032.60 de Visibility=Nein; R. Nussbaum AG 90032.65 de Visibility=Nein; R. Nussbaum AG 90032.70 de Visibility=Nein; R. Nussbaum AG 90032.80 de Visibility=Nein; R. Nussbaum AG 90032.81 de Visibility=Nein; R. Nussbaum AG 90032.88 de Visibility=Nein; R. Nussbaum AG 90032.93 de Visibility=Nein; R. Nussbaum AG 90032.98 de Visibility=Nein; R. Nussbaum AG 90032.99 de Visibility=Nein; Typenkommentare=Optifitt-Serra-Rohrnippel  DN=15; URL=https://www.nussbaum.ch
- DN=10: 1.800.00.3 TGA-Nummer=01900300000000000000000000000000000000000000000019000000000000000016; 1.800.00.4 Kommentarfeld=90032.47, Optifitt-Serra-Rohrnippel, DN=15, L=160, R=½; 1.810.00.3 Hersteller-Bestellnummer=90032.47; 1.810.00.4 DATANORM-Nummer=90032.47; 1.810.00.6 GTIN-Nummer=7612945034298; 29.710.02.10 Formstück-Gewicht [kg]=0.264; 29.710.02.3 Benennung=Optifitt-Serra-Rohrnippel, DN=15, L=160, R=½; CONNECTOR0_DIAMETER_dX_0r=15 mm  [stored 0.0492126 ft]; CONNECTOR0_dX_01=13 mm; CONNECTOR0_ref_dX=13 mm; CONNECTOR1_DIAMETER_dX_0r=15 mm  [stored 0.0492126 ft]; CONNECTOR1_dX_00=145 mm; CONNECTOR1_dX_01=158 mm; CONNECTOR1_ref_dX=145 mm; CONNECTOR1_ref_dX2=158 mm; Hersteller=R. Nussbaum AG; Modell=90032.47; R. Nussbaum AG 90032.36 de Visibility=Nein; R. Nussbaum AG 90032.37 de Visibility=Nein; R. Nussbaum AG 90032.40 de Visibility=Nein; R. Nussbaum AG 90032.47 de Visibility=Ja; R. Nussbaum AG 90032.48 de Visibility=Nein; R. Nussbaum AG 90032.50 de Visibility=Nein; R. Nussbaum AG 90032.55 de Visibility=Nein; R. Nussbaum AG 90032.57 de Visibility=Nein; R. Nussbaum AG 90032.60 de Visibility=Nein; R. Nussbaum AG 90032.65 de Visibility=Nein; R. Nussbaum AG 90032.70 de Visibility=Nein; R. Nussbaum AG 90032.80 de Visibility=Nein; R. Nussbaum AG 90032.81 de Visibility=Nein; R. Nussbaum AG 90032.88 de Visibility=Nein; R. Nussbaum AG 90032.93 de Visibility=Nein; R. Nussbaum AG 90032.98 de Visibility=Nein; R. Nussbaum AG 90032.99 de Visibility=Nein; Typenkommentare=Optifitt-Serra-Rohrnippel  DN=15; URL=https://www.nussbaum.ch
- DN=1: 1.800.00.3 TGA-Nummer=01900300000000000000000000000000000000000000000019000000000000000007; 1.800.00.4 Kommentarfeld=90032.36, Optifitt-Serra-Rohrnippel, DN=15, L=40, R=½; 1.810.00.3 Hersteller-Bestellnummer=90032.36; 1.810.00.4 DATANORM-Nummer=90032.36; 1.810.00.5 StLB-Nummer=214.232; 1.810.00.6 GTIN-Nummer=7612945034229; 29.710.02.10 Formstück-Gewicht [kg]=0.056; 29.710.02.3 Benennung=Optifitt-Serra-Rohrnippel, DN=15, L=40, R=½; CONNECTOR0_DIAMETER_dX_0r=15 mm  [stored 0.0492126 ft]; CONNECTOR0_dX_01=13 mm; CONNECTOR0_ref_dX=13 mm; CONNECTOR1_DIAMETER_dX_0r=15 mm  [stored 0.0492126 ft]; CONNECTOR1_dX_00=25 mm  [stored 0.082021 ft]; CONNECTOR1_dX_01=38 mm; CONNECTOR1_ref_dX=25 mm  [stored 0.082021 ft]; CONNECTOR1_ref_dX2=38 mm; Hersteller=R. Nussbaum AG; Modell=90032.36; R. Nussbaum AG 90032.36 de Visibility=Ja; R. Nussbaum AG 90032.37 de Visibility=Nein; R. Nussbaum AG 90032.40 de Visibility=Nein; R. Nussbaum AG 90032.47 de Visibility=Nein; R. Nussbaum AG 90032.48 de Visibility=Nein; R. Nussbaum AG 90032.50 de Visibility=Nein; R. Nussbaum AG 90032.55 de Visibility=Nein; R. Nussbaum AG 90032.57 de Visibility=Nein; R. Nussbaum AG 90032.60 de Visibility=Nein; R. Nussbaum AG 90032.65 de Visibility=Nein; R. Nussbaum AG 90032.70 de Visibility=Nein; R. Nussbaum AG 90032.80 de Visibility=Nein; R. Nussbaum AG 90032.81 de Visibility=Nein; R. Nussbaum AG 90032.88 de Visibility=Nein; R. Nussbaum AG 90032.93 de Visibility=Nein; R. Nussbaum AG 90032.98 de Visibility=Nein; R. Nussbaum AG 90032.99 de Visibility=Nein; Typenkommentare=Optifitt-Serra-Rohrnippel  DN=15; URL=https://www.nussbaum.ch

note: [stored X ft] marks values corroborated as IEEE doubles in the binary element streams (Revit-internal decimal feet)

## geometry (parser evidence)
native form markers: Sweep x2
no freeform markers — native parametric forms only
